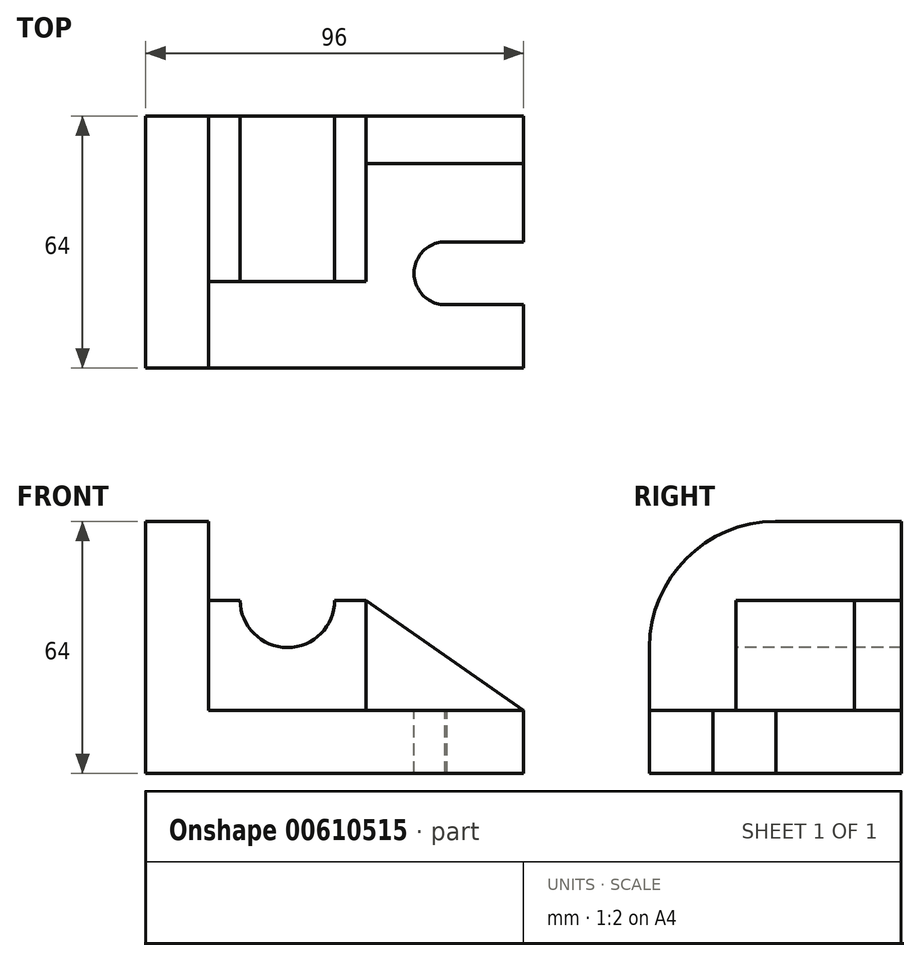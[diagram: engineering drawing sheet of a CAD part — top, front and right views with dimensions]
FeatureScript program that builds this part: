
annotation { "Feature Type Name" : "Feature", "Feature Type Description" : "" }
export const myFeature = defineFeature(function(context is Context, id is Id, definition is map)
    precondition{}
    {
        {
            var Q0;
            Q0=qCreatedBy(makeId("Top.planeOp"),FACE);
            var sketch = newSketch(context, id + "F0", { "sketchPlane" : qUnion([Q0])});
            skLineSegment(sketch, "E0.bottom", {"start": v(-43.06, 42.7) * mm, "end": v(52.94, 42.7) * mm});
            skLineSegment(sketch, "E0.top", {"start": v(-43.06, -21.3) * mm, "end": v(52.94, -21.3) * mm});
            skLineSegment(sketch, "E0.left", {"start": v(-43.06, 42.7) * mm, "end": v(-43.06, -21.3) * mm});
            skLineSegment(sketch, "E0.right", {"start": v(52.94, 42.7) * mm, "end": v(52.94, -21.3) * mm});
            skSolve(sketch);
        }
        {
            var Q0;
            Q0=makeQuery(id+"F0.imprint","IMPRINT",FACE,{"disambiguationData":[TD([[makeQuery(id+"F0.imprint","IMPRINT",EDGE,{"derivedFrom":sQuery(id+"F0.wireOp",EDGE,"E0.bottom")}),-1.0]])]});
            extrude(context, id + "F1", {"entities" : qUnion([Q0]), "depth" : 16 * mm, "offsetDistance" : 25.4 * mm});
        }
        {
            var Q0;
            Q0=makeQuery(id+"F1.opExtrude","CAP_FACE",FACE,{"disambiguationData":[OSD([sQuery(id+"F0.wireOp",EDGE,"E0.bottom"),sQuery(id+"F0.wireOp",EDGE,"E0.top"),sQuery(id+"F0.wireOp",EDGE,"E0.left"),sQuery(id+"F0.wireOp",EDGE,"E0.right")])],"isStart":false});
            var sketch = newSketch(context, id + "F2", { "sketchPlane" : qUnion([Q0])});
            skLineSegment(sketch, "E1.bottom", {"start": v(-43.06, 42.7) * mm, "end": v(-27.06, 42.7) * mm});
            skLineSegment(sketch, "E1.top", {"start": v(-43.06, -21.3) * mm, "end": v(-27.06, -21.3) * mm});
            skLineSegment(sketch, "E1.left", {"start": v(-43.06, 42.7) * mm, "end": v(-43.06, -21.3) * mm});
            skLineSegment(sketch, "E1.right", {"start": v(-27.06, 42.7) * mm, "end": v(-27.06, -21.3) * mm});
            skSolve(sketch);
        }
        {
            var Q0;
            Q0=makeQuery(id+"F2.imprint","IMPRINT",FACE,{"disambiguationData":[TD([[makeQuery(id+"F2.imprint","IMPRINT",EDGE,{"derivedFrom":sQuery(id+"F2.wireOp",EDGE,"E1.bottom")}),-1.0]])]});
            extrude(context, id + "F3", {"entities" : qUnion([Q0]), "operationType" : NewBodyOperationType.ADD, "depth" : 48 * mm, "offsetDistance" : 25.4 * mm});
        }
        {
            var Q0;
            Q0=makeQuery(id+"F3.opExtrude","CAP_EDGE",EDGE,{"disambiguationData":[OSD([sQuery(id+"F2.wireOp",EDGE,"E1.top")])],"isStart":false});
            fillet(context, id + "F4", {"entities" : qUnion([Q0]), "radius" : 32 * mm, "tangentPropagation" : true, "allowEdgeOverflow" : false});
        }
        {
            var Q0;
            Q0=makeQuery(id+"F1.opExtrude","CAP_FACE",FACE,{"disambiguationData":[OSD([sQuery(id+"F0.wireOp",EDGE,"E0.bottom"),sQuery(id+"F0.wireOp",EDGE,"E0.top"),sQuery(id+"F0.wireOp",EDGE,"E0.left"),sQuery(id+"F0.wireOp",EDGE,"E0.right")])],"isStart":false});
            var sketch = newSketch(context, id + "F5", { "sketchPlane" : qUnion([Q0])});
            skLineSegment(sketch, "E2.bottom", {"start": v(-27.06, 42.7) * mm, "end": v(12.94, 42.7) * mm});
            skLineSegment(sketch, "E2.top", {"start": v(-27.06, 0.7) * mm, "end": v(12.94, 0.7) * mm});
            skLineSegment(sketch, "E2.left", {"start": v(-27.06, 42.7) * mm, "end": v(-27.06, 0.7) * mm});
            skLineSegment(sketch, "E2.right", {"start": v(12.94, 42.7) * mm, "end": v(12.94, 0.7) * mm});
            skSolve(sketch);
        }
        {
            var Q0;
            Q0=makeQuery(id+"F5.imprint","IMPRINT",FACE,{"disambiguationData":[TD([[makeQuery(id+"F5.imprint","IMPRINT",EDGE,{"derivedFrom":sQuery(id+"F5.wireOp",EDGE,"E2.bottom")}),-1.0]])]});
            extrude(context, id + "F6", {"entities" : qUnion([Q0]), "operationType" : NewBodyOperationType.ADD, "depth" : 28 * mm, "offsetDistance" : 25.4 * mm});
        }
        {
            var Q0;
            Q0=makeQuery(id+"F6.opExtrude","SWEPT_FACE",FACE,{"disambiguationData":[OSD([sQuery(id+"F5.wireOp",EDGE,"E2.top")])]});
            var sketch = newSketch(context, id + "F7", { "sketchPlane" : qUnion([Q0])});
            skCircle(sketch, "E3", {"center": v(-7.06, 44) * mm, "radius": 12 * mm});
            skSolve(sketch);
        }
        {
            var Q0;
            {var subQ0=sQuery(id+"F7.wireOp",EDGE,"E3");var subQ1=makeQuery(id+"F6.opExtrude","CAP_EDGE",EDGE,{"disambiguationData":[OSD([sQuery(id+"F5.wireOp",EDGE,"E2.top")])],"isStart":false});var subQ2=makeQuery(id+"F7.imprint","INTERSECT",VERTEX,{"disambiguationData":[OD(0.0)],"derivedFrom":[subQ1,subQ0]});Q0=makeQuery(id+"F7.imprint","IMPRINT",FACE,{"disambiguationData":[TD([[makeQuery(id+"F7.imprint","IMPRINT",EDGE,{"disambiguationData":[TD([[subQ2,1.0]])],"derivedFrom":subQ0}),1.0]])]});}
            extrude(context, id + "F8", {"entities" : qUnion([Q0]), "operationType" : NewBodyOperationType.REMOVE, "oppositeDirection" : true, "depth" : 52.07 * mm, "offsetDistance" : 25.4 * mm});
        }
        {
            var Q0;
            Q0=makeQuery(id+"F1.opExtrude","CAP_FACE",FACE,{"disambiguationData":[OSD([sQuery(id+"F0.wireOp",EDGE,"E0.bottom"),sQuery(id+"F0.wireOp",EDGE,"E0.top"),sQuery(id+"F0.wireOp",EDGE,"E0.left"),sQuery(id+"F0.wireOp",EDGE,"E0.right")])],"isStart":false});
            var sketch = newSketch(context, id + "F9", { "sketchPlane" : qUnion([Q0])});
            skLineSegment(sketch, "E4.bottom", {"start": v(12.94, 42.7) * mm, "end": v(52.94, 42.7) * mm});
            skLineSegment(sketch, "E4.top", {"start": v(12.94, 30.7) * mm, "end": v(52.94, 30.7) * mm});
            skLineSegment(sketch, "E4.left", {"start": v(12.94, 42.7) * mm, "end": v(12.94, 30.7) * mm});
            skLineSegment(sketch, "E4.right", {"start": v(52.94, 42.7) * mm, "end": v(52.94, 30.7) * mm});
            skSolve(sketch);
        }
        {
            var Q0;
            Q0=makeQuery(id+"F9.imprint","IMPRINT",FACE,{"disambiguationData":[TD([[makeQuery(id+"F9.imprint","IMPRINT",EDGE,{"derivedFrom":sQuery(id+"F9.wireOp",EDGE,"E4.bottom")}),-1.0]])]});
            extrude(context, id + "F10", {"entities" : qUnion([Q0]), "operationType" : NewBodyOperationType.ADD, "depth" : 28 * mm, "offsetDistance" : 25.4 * mm});
        }
        {
            var Q0;
            Q0=makeQuery(id+"F10.opExtrude","SWEPT_FACE",FACE,{"disambiguationData":[OSD([sQuery(id+"F9.wireOp",EDGE,"E4.top")])]});
            var sketch = newSketch(context, id + "F11", { "sketchPlane" : qUnion([Q0])});
            skLineSegment(sketch, "E5", {"start": v(12.94, 44) * mm, "end": v(52.94, 16) * mm});
            skSolve(sketch);
        }
        {
            var Q0;
            Q0=makeQuery(id+"F11.imprint","IMPRINT",FACE,{"disambiguationData":[TD([[makeQuery(id+"F11.imprint","IMPRINT",EDGE,{"derivedFrom":sQuery(id+"F11.wireOp",EDGE,"E5")}),1.0]])]});
            extrude(context, id + "F12", {"entities" : qUnion([Q0]), "operationType" : NewBodyOperationType.REMOVE, "oppositeDirection" : true, "depth" : 25.4 * mm, "offsetDistance" : 25.4 * mm});
        }
        {
            var Q0;
            Q0=makeQuery(id+"F1.opExtrude","CAP_FACE",FACE,{"disambiguationData":[OSD([sQuery(id+"F0.wireOp",EDGE,"E0.bottom"),sQuery(id+"F0.wireOp",EDGE,"E0.top"),sQuery(id+"F0.wireOp",EDGE,"E0.left"),sQuery(id+"F0.wireOp",EDGE,"E0.right")])],"isStart":false});
            var sketch = newSketch(context, id + "F13", { "sketchPlane" : qUnion([Q0])});
            skLineSegment(sketch, "E6.bottom", {"start": v(52.94, -21.23) * mm, "end": v(32.94, -21.23) * mm});
            skLineSegment(sketch, "E6.top", {"start": v(52.94, -5.23) * mm, "end": v(32.94, -5.23) * mm});
            skLineSegment(sketch, "E6.left", {"start": v(52.94, -21.23) * mm, "end": v(52.94, -5.23) * mm});
            skLineSegment(sketch, "E6.right", {"start": v(32.94, -21.23) * mm, "end": v(32.94, -5.23) * mm});
            skSolve(sketch);
        }
        {
            var Q0;
            {var subQ2=sQuery(id+"F13.wireOp",EDGE,"E6.bottom");Q0=makeQuery(id+"F13.imprint","IMPRINT",FACE,{"disambiguationData":[TD([[makeQuery(id+"F13.imprint","IMPRINT",EDGE,{"derivedFrom":subQ2}),1.0]])]});}
            var sketch = newSketch(context, id + "F14", { "sketchPlane" : qUnion([Q0])});
            skLineSegment(sketch, "E7.bottom", {"start": v(53.02, -5.24) * mm, "end": v(33.02, -5.24) * mm});
            skLineSegment(sketch, "E7.top", {"start": v(53.02, 10.76) * mm, "end": v(33.02, 10.76) * mm});
            skLineSegment(sketch, "E7.left", {"start": v(53.02, -5.24) * mm, "end": v(53.02, 10.76) * mm});
            skLineSegment(sketch, "E7.right", {"start": v(33.02, -5.24) * mm, "end": v(33.02, 10.76) * mm});
            skSolve(sketch);
        }
        {
            var Q0;
            {var subQ0=sQuery(id+"F14.wireOp",EDGE,"E7.right");Q0=makeQuery(id+"F14.imprint","IMPRINT",FACE,{"disambiguationData":[TD([[makeQuery(id+"F14.imprint","IMPRINT",EDGE,{"derivedFrom":subQ0}),-1.0]])]});}
            extrude(context, id + "F15", {"entities" : qUnion([Q0]), "operationType" : NewBodyOperationType.REMOVE, "oppositeDirection" : true, "depth" : 25 * mm, "offsetDistance" : 25 * mm});
        }
        {
            var Q0;
            {var subQ5=sQuery(id+"F13.wireOp",EDGE,"E6.bottom");Q0=makeQuery(id+"F14.imprint","IMPRINT",FACE,{"disambiguationData":[TD([[makeQuery(id+"F14.imprint","IMPRINT",EDGE,{"derivedFrom":makeQuery(id+"F13.imprint","IMPRINT",EDGE,{"derivedFrom":subQ5})}),1.0]])]});}
            var sketch = newSketch(context, id + "F16", { "sketchPlane" : qUnion([Q0])});
            skCircle(sketch, "E8", {"center": v(33.11, 2.77) * mm, "radius": 8 * mm});
            skSolve(sketch);
        }
        {
            var Q0;
            {var subQ0=sQuery(id+"F14.wireOp",EDGE,"E7.right");var subQ1=sQuery(id+"F14.wireOp",EDGE,"E7.top");var subQ2=makeQuery(id+"F14.imprint","INTERSECT",VERTEX,{"derivedFrom":[subQ1,subQ0]});var subQ6=makeQuery(id+"F14.imprint","IMPRINT",EDGE,{"disambiguationData":[TD([[subQ2,1.0]])],"derivedFrom":subQ0});Q0=makeQuery(id+"F16.imprint","IMPRINT",FACE,{"disambiguationData":[TD([[makeQuery(id+"F16.imprint","IMPRINT",EDGE,{"derivedFrom":subQ6}),1.0]])]});}
            extrude(context, id + "F17", {"entities" : qUnion([Q0]), "operationType" : NewBodyOperationType.REMOVE, "oppositeDirection" : true, "depth" : 25 * mm, "offsetDistance" : 25 * mm});
        }
    });
